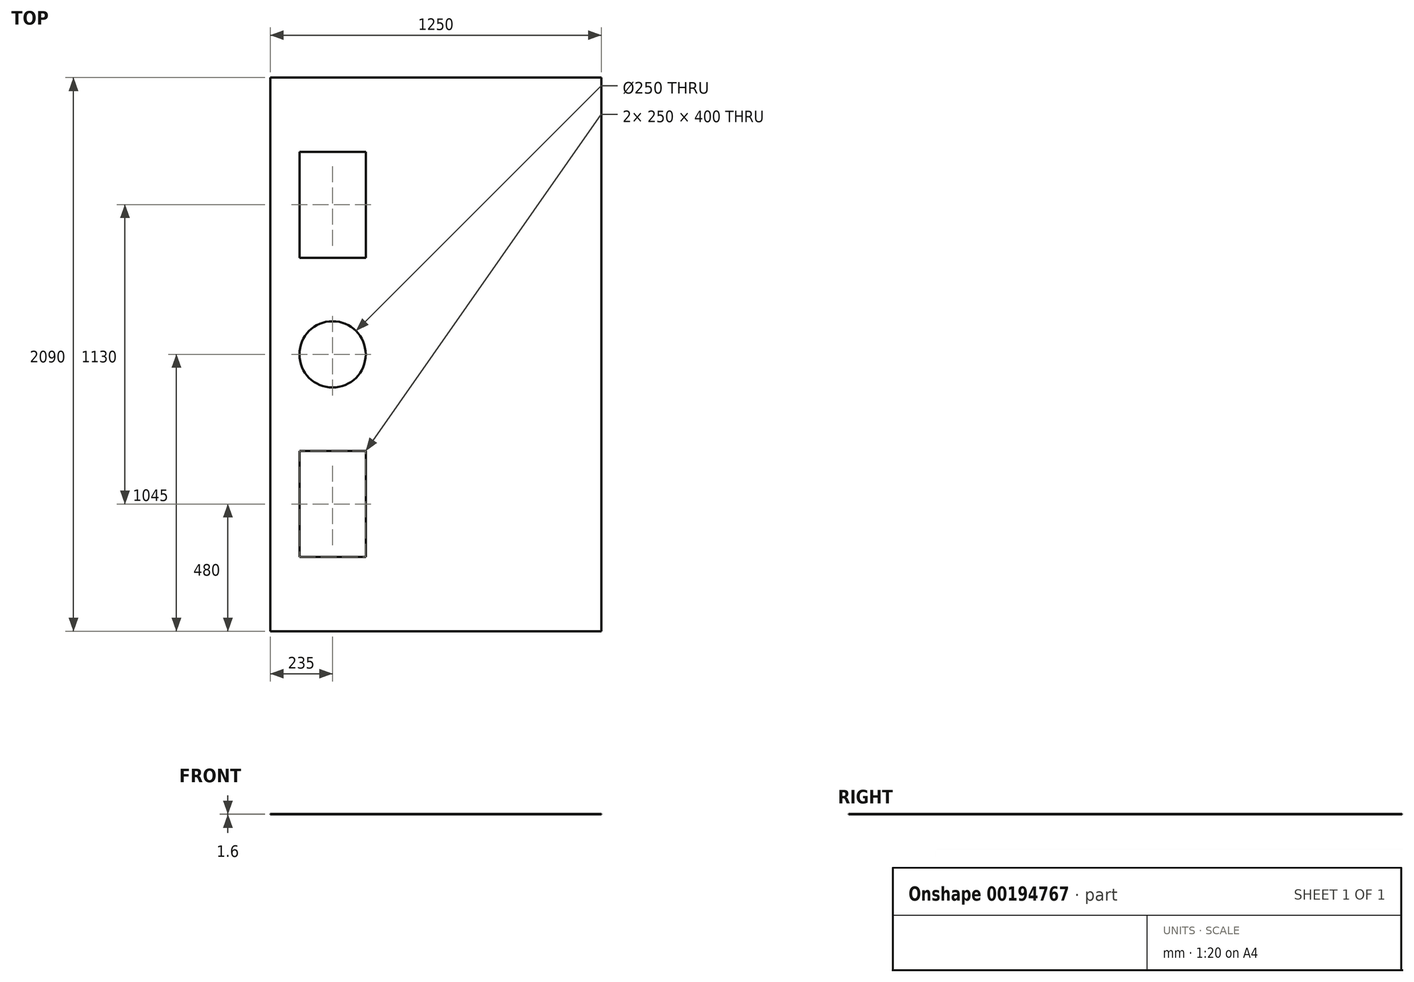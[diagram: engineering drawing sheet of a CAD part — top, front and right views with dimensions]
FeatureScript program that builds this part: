
annotation { "Feature Type Name" : "Feature", "Feature Type Description" : "" }
export const myFeature = defineFeature(function(context is Context, id is Id, definition is map)
    precondition{}
    {
        {
            var Q0;
            Q0=qCreatedBy(makeId("Top.planeOp"),FACE);
            var sketch = newSketch(context, id + "F0", { "sketchPlane" : qUnion([Q0])});
            skLineSegment(sketch, "E0.bottom", {"start": v(625, 1045) * mm, "end": v(-625, 1045) * mm});
            skLineSegment(sketch, "E0.top", {"start": v(625, -1045) * mm, "end": v(-625, -1045) * mm});
            skLineSegment(sketch, "E0.left", {"start": v(625, 1045) * mm, "end": v(625, -1045) * mm});
            skLineSegment(sketch, "E0.right", {"start": v(-625, 1045) * mm, "end": v(-625, -1045) * mm});
            skPoint(sketch, "E0.middle", {"position": v(0, 0) * mm});
            skLineSegment(sketch, "E1.bottom", {"start": v(-265, 365) * mm, "end": v(-515, 365) * mm});
            skLineSegment(sketch, "E1.top", {"start": v(-265, 765) * mm, "end": v(-515, 765) * mm});
            skLineSegment(sketch, "E1.left", {"start": v(-265, 365) * mm, "end": v(-265, 765) * mm});
            skLineSegment(sketch, "E1.right", {"start": v(-515, 365) * mm, "end": v(-515, 765) * mm});
            skPoint(sketch, "E1.middle", {"position": v(-390, 565) * mm});
            skLineSegment(sketch, "E2.bottom", {"start": v(-265, -365) * mm, "end": v(-515, -365) * mm});
            skLineSegment(sketch, "E2.top", {"start": v(-265, -765) * mm, "end": v(-515, -765) * mm});
            skLineSegment(sketch, "E2.left", {"start": v(-265, -365) * mm, "end": v(-265, -765) * mm});
            skLineSegment(sketch, "E2.right", {"start": v(-515, -365) * mm, "end": v(-515, -765) * mm});
            skPoint(sketch, "E2.middle", {"position": v(-390, -565) * mm});
            skPoint(sketch, "E2.middle.positionSnap0", {"position": v(-390, 365) * mm});
            skPoint(sketch, "E2.centerSnap0", {"position": v(-390, 365) * mm});
            skCircle(sketch, "E3", {"center": v(-390, 0) * mm, "radius": 125 * mm});
            skSolve(sketch);
        }
        {
            var Q0;
            Q0 = qSketchRegion(id + "F0", true);
            extrude(context, id + "F1", {"entities" : qUnion([Q0]), "depth" : 1.6 * mm});
        }
    });
